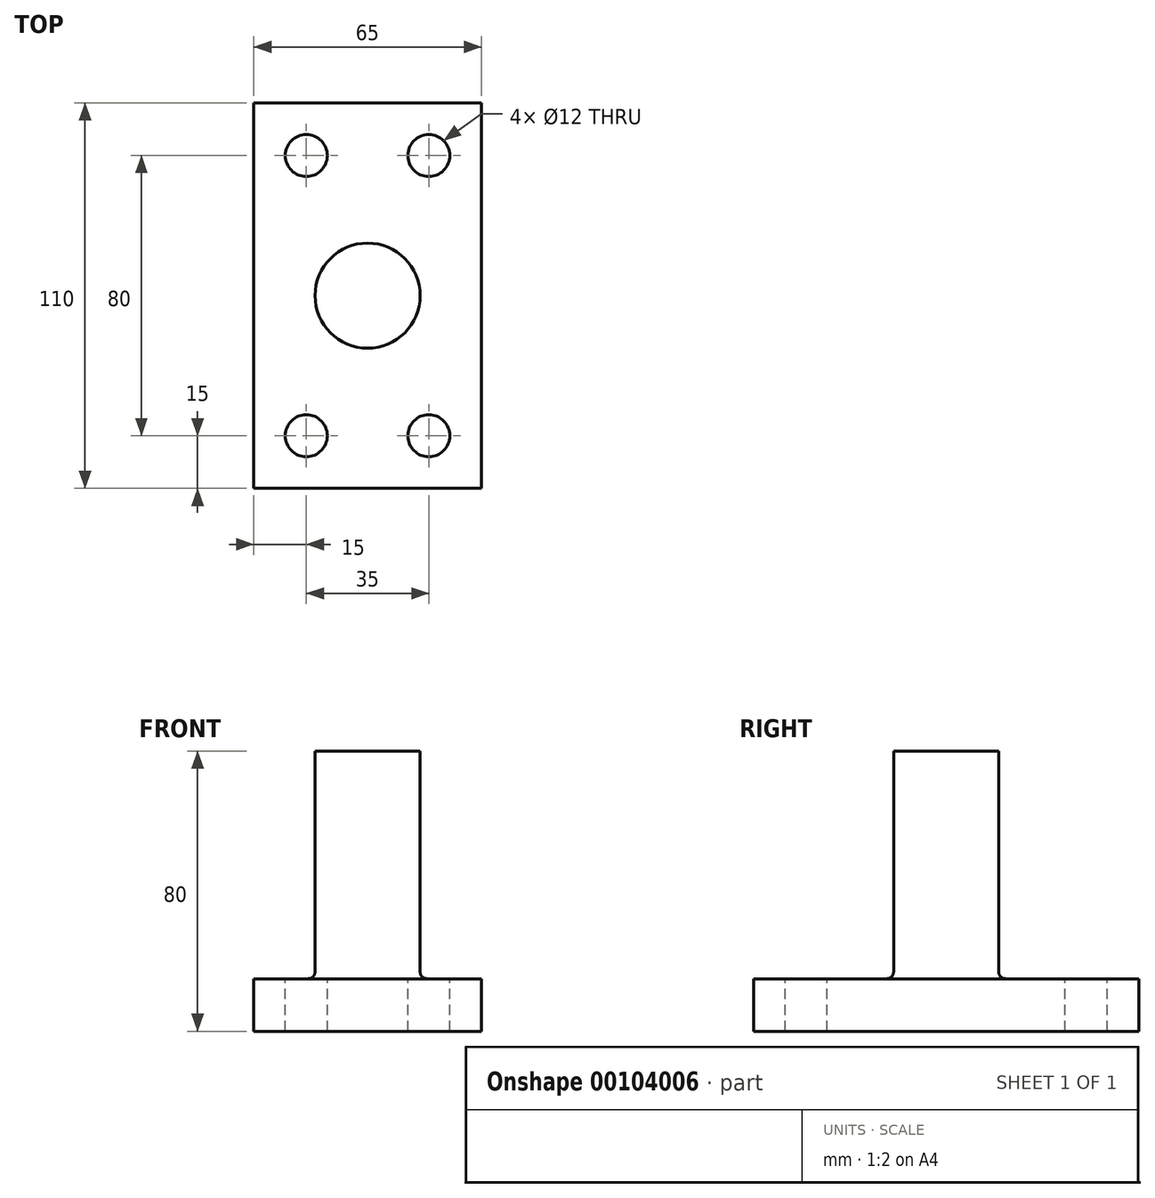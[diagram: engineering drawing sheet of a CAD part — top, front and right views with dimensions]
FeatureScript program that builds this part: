
annotation { "Feature Type Name" : "Feature", "Feature Type Description" : "" }
export const myFeature = defineFeature(function(context is Context, id is Id, definition is map)
    precondition{}
    {
        {
            var Q0;
            Q0=qCreatedBy(makeId("Top.planeOp"),FACE);
            var sketch = newSketch(context, id + "F0", { "sketchPlane" : qUnion([Q0])});
            skLineSegment(sketch, "E0.bottom", {"start": v(-32.5, 55) * mm, "end": v(32.5, 55) * mm});
            skLineSegment(sketch, "E0.top", {"start": v(-32.5, -55) * mm, "end": v(32.5, -55) * mm});
            skLineSegment(sketch, "E0.left", {"start": v(-32.5, 55) * mm, "end": v(-32.5, -55) * mm});
            skLineSegment(sketch, "E0.right", {"start": v(32.5, 55) * mm, "end": v(32.5, -55) * mm});
            skPoint(sketch, "E0.middle", {"position": v(0, 0) * mm});
            skSolve(sketch);
        }
        {
            var Q0;
            Q0=makeQuery(id+"F0.imprint","IMPRINT",FACE,{"disambiguationData":[TD([[makeQuery(id+"F0.imprint","IMPRINT",EDGE,{"derivedFrom":sQuery(id+"F0.wireOp",EDGE,"E0.bottom")}),-1.0]])]});
            extrude(context, id + "F1", {"entities" : qUnion([Q0]), "depth" : 100 * mm});
        }
        {
            var Q0;
            Q0=makeQuery(id+"F1.opExtrude","CAP_FACE",FACE,{"disambiguationData":[OSD([sQuery(id+"F0.wireOp",EDGE,"E0.bottom"),sQuery(id+"F0.wireOp",EDGE,"E0.top"),sQuery(id+"F0.wireOp",EDGE,"E0.left"),sQuery(id+"F0.wireOp",EDGE,"E0.right")])],"isStart":false});
            var sketch = newSketch(context, id + "F2", { "sketchPlane" : qUnion([Q0])});
            skCircle(sketch, "E1", {"center": v(0, 0) * mm, "radius": 15 * mm});
            skSolve(sketch);
        }
        {
            var Q0;
            Q0=makeQuery(id+"F2.imprint","IMPRINT",FACE,{"disambiguationData":[TD([[makeQuery(id+"F2.imprint","IMPRINT",EDGE,{"derivedFrom":sQuery(id+"F2.wireOp",EDGE,"E1")}),-1.0]])]});
            extrude(context, id + "F3", {"entities" : qUnion([Q0]), "operationType" : NewBodyOperationType.REMOVE, "oppositeDirection" : true, "depth" : 85 * mm});
        }
        {
            var Q0;
            Q0=makeQuery(id+"F1.opExtrude","CAP_FACE",FACE,{"disambiguationData":[OSD([sQuery(id+"F0.wireOp",EDGE,"E0.bottom"),sQuery(id+"F0.wireOp",EDGE,"E0.top"),sQuery(id+"F0.wireOp",EDGE,"E0.left"),sQuery(id+"F0.wireOp",EDGE,"E0.right")])],"isStart":false});
            extrude(context, id + "F4", {"entities" : qUnion([Q0]), "operationType" : NewBodyOperationType.REMOVE, "oppositeDirection" : true, "depth" : 20 * mm});
        }
        {
            var Q0;
            Q0=makeQuery(id+"F3.boolean.opBoolean","COPY",FACE,{"derivedFrom":makeQuery(id+"F3.opExtrude","CAP_FACE",FACE,{"disambiguationData":[OSD([sQuery(id+"F0.wireOp",EDGE,"E0.bottom"),sQuery(id+"F0.wireOp",EDGE,"E0.top"),sQuery(id+"F0.wireOp",EDGE,"E0.left"),sQuery(id+"F0.wireOp",EDGE,"E0.right"),sQuery(id+"F2.wireOp",EDGE,"E1")])],"isStart":false})});
            var sketch = newSketch(context, id + "F5", { "sketchPlane" : qUnion([Q0])});
            skCircle(sketch, "E2", {"center": v(-17.5, 40) * mm, "radius": 6 * mm});
            skCircle(sketch, "E3", {"center": v(17.5, 40) * mm, "radius": 6 * mm});
            skCircle(sketch, "E4", {"center": v(-17.5, -40) * mm, "radius": 6 * mm});
            skCircle(sketch, "E5", {"center": v(17.5, -40) * mm, "radius": 6 * mm});
            skCircle(sketch, "E6", {"center": v(0, 0) * mm, "radius": 2.5 * mm});
            skSolve(sketch);
        }
        {
            var Q0;
            Q0=makeQuery(id+"F5.imprint","IMPRINT",FACE,{"disambiguationData":[TD([[makeQuery(id+"F5.imprint","IMPRINT",EDGE,{"derivedFrom":sQuery(id+"F5.wireOp",EDGE,"E2")}),1.0]])]});
            var Q1;
            Q1=makeQuery(id+"F5.imprint","IMPRINT",FACE,{"disambiguationData":[TD([[makeQuery(id+"F5.imprint","IMPRINT",EDGE,{"derivedFrom":sQuery(id+"F5.wireOp",EDGE,"E3")}),1.0]])]});
            var Q2;
            Q2=makeQuery(id+"F5.imprint","IMPRINT",FACE,{"disambiguationData":[TD([[makeQuery(id+"F5.imprint","IMPRINT",EDGE,{"derivedFrom":sQuery(id+"F5.wireOp",EDGE,"E5")}),1.0]])]});
            var Q3;
            Q3=makeQuery(id+"F5.imprint","IMPRINT",FACE,{"disambiguationData":[TD([[makeQuery(id+"F5.imprint","IMPRINT",EDGE,{"derivedFrom":sQuery(id+"F5.wireOp",EDGE,"E4")}),1.0]])]});
            extrude(context, id + "F6", {"entities" : qUnion([Q0, Q1, Q2, Q3]), "operationType" : NewBodyOperationType.REMOVE, "oppositeDirection" : true, "depth" : 30 * mm});
        }
        {
            var Q0;
            Q0=makeQuery(id+"F4.boolean.opBoolean","COPY",EDGE,{"derivedFrom":makeQuery(id+"F4.opExtrude","CAP_EDGE",EDGE,{"disambiguationData":[OSD([sQuery(id+"F2.wireOp",EDGE,"E1")])],"isStart":false})});
            var Q1;
            Q1=makeQuery(id+"F3.boolean.opBoolean","COPY",EDGE,{"derivedFrom":makeQuery(id+"F3.opExtrude","CAP_EDGE",EDGE,{"disambiguationData":[OSD([sQuery(id+"F2.wireOp",EDGE,"E1")])],"isStart":false})});
            fillet(context, id + "F7", {"entities" : qUnion([Q0, Q1]), "radius" : 2 * mm, "tangentPropagation" : true, "allowEdgeOverflow" : false});
        }
    });
